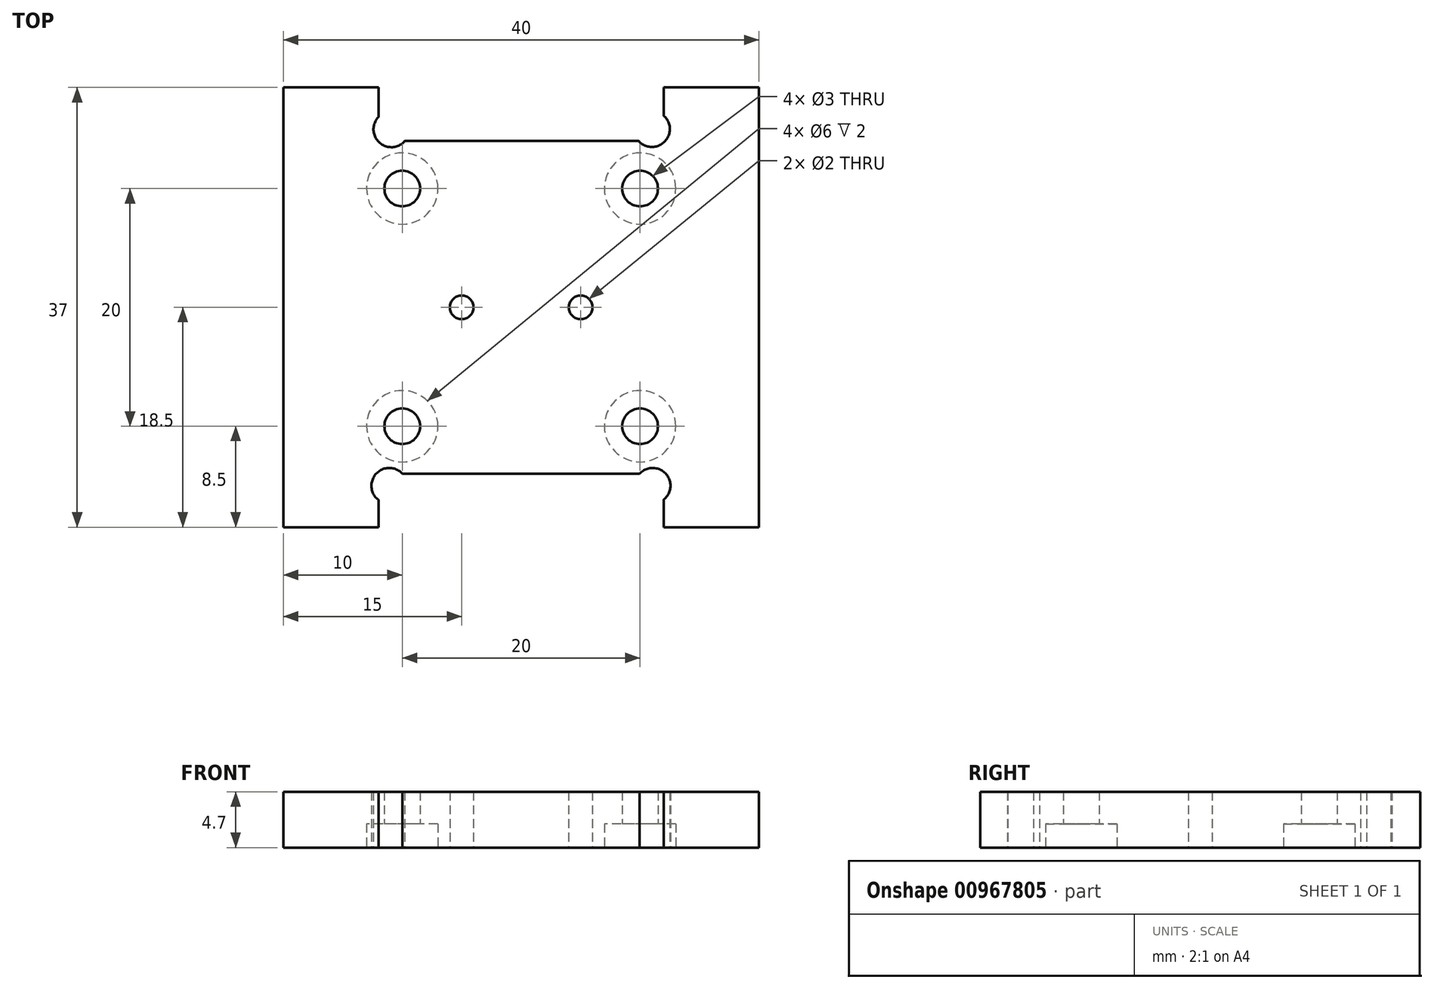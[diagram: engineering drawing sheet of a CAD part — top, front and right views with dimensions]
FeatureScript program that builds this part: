
annotation { "Feature Type Name" : "Feature", "Feature Type Description" : "" }
export const myFeature = defineFeature(function(context is Context, id is Id, definition is map)
    precondition{}
    {
        {
            var Q0;
            Q0=qCreatedBy(makeId("Top.planeOp"),FACE);
            var sketch = newSketch(context, id + "F0", { "sketchPlane" : qUnion([Q0])});
            skPoint(sketch, "E0.middle", {"position": v(0, 0) * mm});
            skCircle(sketch, "E1", {"center": v(10, 10) * mm, "radius": 1.5 * mm});
            skCircle(sketch, "E2", {"center": v(10, 10) * mm, "radius": 3 * mm});
            skCircle(sketch, "E3", {"center": v(-10, 10) * mm, "radius": 1.5 * mm});
            skCircle(sketch, "E4", {"center": v(-10, 10) * mm, "radius": 3 * mm});
            skCircle(sketch, "E5", {"center": v(-10, -10) * mm, "radius": 1.5 * mm});
            skCircle(sketch, "E6", {"center": v(-10, -10) * mm, "radius": 3 * mm});
            skCircle(sketch, "E7", {"center": v(10, -10) * mm, "radius": 1.5 * mm});
            skCircle(sketch, "E8", {"center": v(10, -10) * mm, "radius": 3 * mm});
            skCircle(sketch, "E9", {"center": v(5, 0) * mm, "radius": 1 * mm});
            skCircle(sketch, "E10", {"center": v(-5, 0) * mm, "radius": 1 * mm});
            skLineSegment(sketch, "E11.left", {"start": v(20, -18.5) * mm, "end": v(20, 18.5) * mm});
            skLineSegment(sketch, "E11.right", {"start": v(-20, -18.5) * mm, "end": v(-20, 18.5) * mm});
            skLineSegment(sketch, "E12.top", {"start": v(12, -14) * mm, "end": v(-12, -14) * mm});
            skLineSegment(sketch, "E13.bottom", {"start": v(12, 14) * mm, "end": v(-12, 14) * mm});
            skLineSegment(sketch, "E13.left", {"start": v(12, 14) * mm, "end": v(12, 18.5) * mm});
            skLineSegment(sketch, "E13.right", {"start": v(-12, 14) * mm, "end": v(-12, 18.5) * mm});
            skLineSegment(sketch, "E14.left", {"start": v(-12, -14) * mm, "end": v(-12, -18.5) * mm});
            skLineSegment(sketch, "E14.right", {"start": v(12, -14) * mm, "end": v(12, -18.5) * mm});
            skLineSegment(sketch, "E15", {"start": v(-20, 18.5) * mm, "end": v(-12, 18.5) * mm});
            skLineSegment(sketch, "E16", {"start": v(12, 18.5) * mm, "end": v(20, 18.5) * mm});
            skLineSegment(sketch, "E17", {"start": v(20, -18.5) * mm, "end": v(12, -18.5) * mm});
            skLineSegment(sketch, "E18", {"start": v(-12, -18.5) * mm, "end": v(-20, -18.5) * mm});
            skCircle(sketch, "E19", {"center": v(11, 15) * mm, "radius": 1.5 * mm});
            skCircle(sketch, "E20", {"center": v(-10.92, 14.98) * mm, "radius": 1.5 * mm});
            skCircle(sketch, "E21", {"center": v(11.05, -15.01) * mm, "radius": 1.5 * mm});
            skCircle(sketch, "E22", {"center": v(-11.09, -15.01) * mm, "radius": 1.5 * mm});
            skSolve(sketch);
        }
        {
            var Q0;
            Q0=makeQuery(id+"F0.imprint","IMPRINT",FACE,{"disambiguationData":[TD([[makeQuery(id+"F0.imprint","IMPRINT",EDGE,{"derivedFrom":sQuery(id+"F0.wireOp",EDGE,"E2")}),-1.0]])]});
            var Q1;
            Q1=makeQuery(id+"F0.imprint","IMPRINT",FACE,{"disambiguationData":[TD([[makeQuery(id+"F0.imprint","IMPRINT",EDGE,{"derivedFrom":sQuery(id+"F0.wireOp",EDGE,"E1")}),-1.0]])]});
            var Q2;
            Q2=makeQuery(id+"F0.imprint","IMPRINT",FACE,{"disambiguationData":[TD([[makeQuery(id+"F0.imprint","IMPRINT",EDGE,{"derivedFrom":sQuery(id+"F0.wireOp",EDGE,"E3")}),-1.0]])]});
            var Q3;
            Q3=makeQuery(id+"F0.imprint","IMPRINT",FACE,{"disambiguationData":[TD([[makeQuery(id+"F0.imprint","IMPRINT",EDGE,{"derivedFrom":sQuery(id+"F0.wireOp",EDGE,"E5")}),-1.0]])]});
            var Q4;
            Q4=makeQuery(id+"F0.imprint","IMPRINT",FACE,{"disambiguationData":[TD([[makeQuery(id+"F0.imprint","IMPRINT",EDGE,{"derivedFrom":sQuery(id+"F0.wireOp",EDGE,"E7")}),-1.0]])]});
            extrude(context, id + "F1", {"entities" : qUnion([Q0, Q1, Q2, Q3, Q4]), "depth" : 4.7 * mm, "offsetDistance" : 25 * mm});
        }
        {
            var Q0;
            Q0=makeQuery(id+"F0.imprint","IMPRINT",FACE,{"disambiguationData":[TD([[makeQuery(id+"F0.imprint","IMPRINT",EDGE,{"derivedFrom":sQuery(id+"F0.wireOp",EDGE,"E1")}),-1.0]])]});
            var Q1;
            Q1=makeQuery(id+"F0.imprint","IMPRINT",FACE,{"disambiguationData":[TD([[makeQuery(id+"F0.imprint","IMPRINT",EDGE,{"derivedFrom":sQuery(id+"F0.wireOp",EDGE,"E3")}),-1.0]])]});
            var Q2;
            Q2=makeQuery(id+"F0.imprint","IMPRINT",FACE,{"disambiguationData":[TD([[makeQuery(id+"F0.imprint","IMPRINT",EDGE,{"derivedFrom":sQuery(id+"F0.wireOp",EDGE,"E7")}),-1.0]])]});
            var Q3;
            Q3=makeQuery(id+"F0.imprint","IMPRINT",FACE,{"disambiguationData":[TD([[makeQuery(id+"F0.imprint","IMPRINT",EDGE,{"derivedFrom":sQuery(id+"F0.wireOp",EDGE,"E5")}),-1.0]])]});
            extrude(context, id + "F2", {"entities" : qUnion([Q0, Q1, Q2, Q3]), "operationType" : NewBodyOperationType.REMOVE, "depth" : 2 * mm, "offsetDistance" : 25 * mm});
        }
    });
